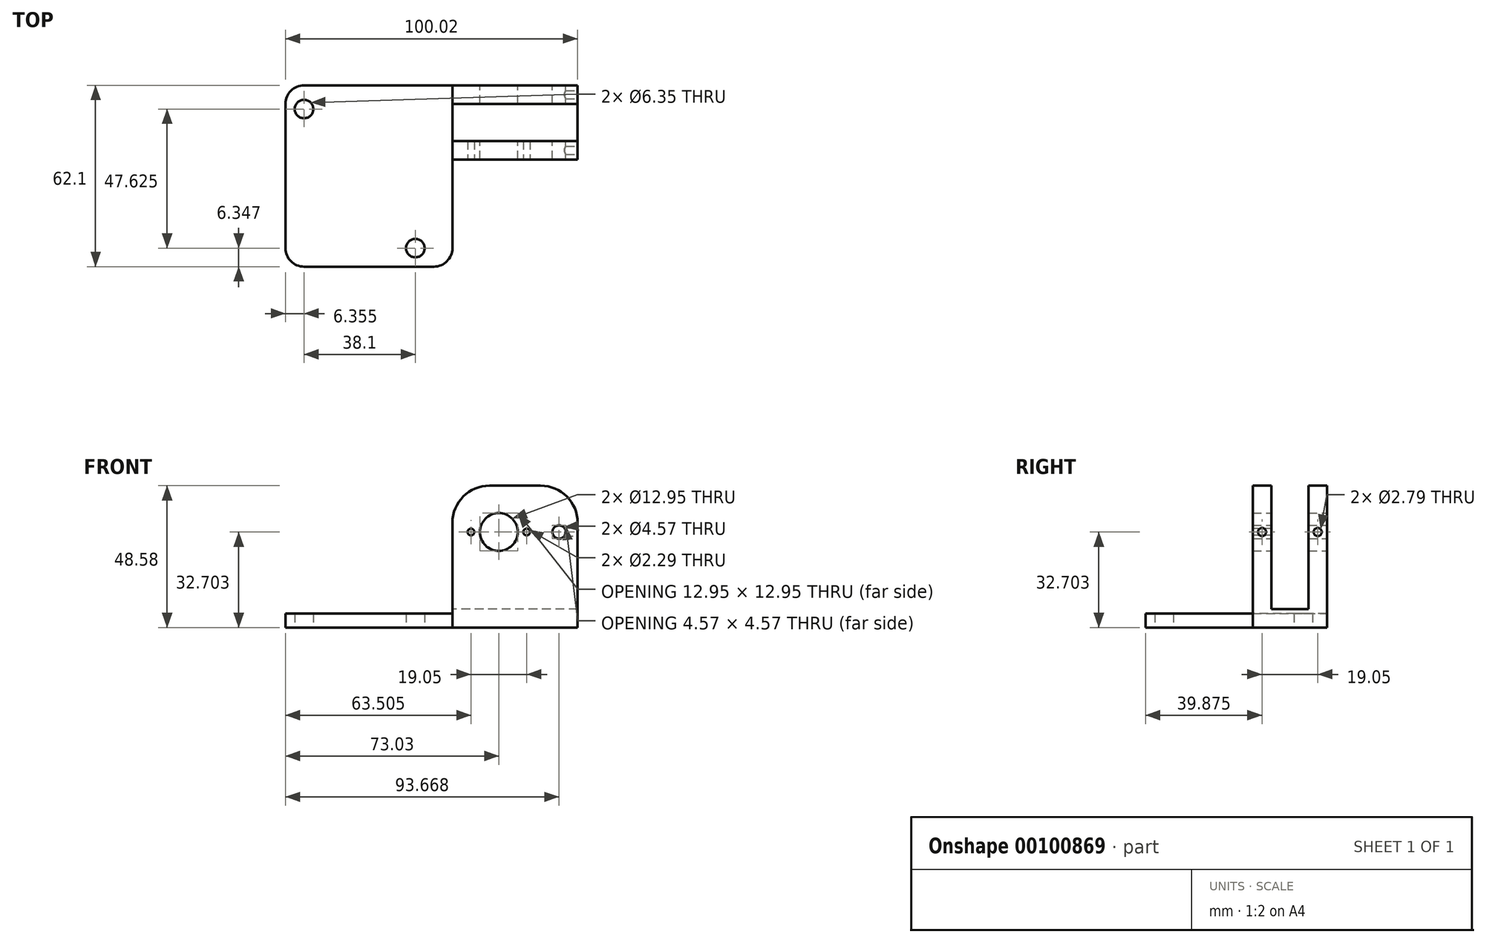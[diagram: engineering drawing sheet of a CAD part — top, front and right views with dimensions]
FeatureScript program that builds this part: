
annotation { "Feature Type Name" : "Feature", "Feature Type Description" : "" }
export const myFeature = defineFeature(function(context is Context, id is Id, definition is map)
    precondition{}
    {
        {
            var Q0;
            Q0=qCreatedBy(makeId("Front.planeOp"),FACE);
            var sketch = newSketch(context, id + "F0", { "sketchPlane" : qUnion([Q0])});
            skCircle(sketch, "E0", {"center": v(0, 32.7) * mm, "radius": 6.48 * mm});
            skLineSegment(sketch, "E1.bottom", {"start": v(-15.87, 0) * mm, "end": v(26.99, 0) * mm});
            skLineSegment(sketch, "E1.top", {"start": v(-3.18, 48.58) * mm, "end": v(14.29, 48.58) * mm});
            skLineSegment(sketch, "E1.left", {"start": v(-15.87, 0) * mm, "end": v(-15.88, 35.88) * mm});
            skLineSegment(sketch, "E1.right", {"start": v(26.99, 0) * mm, "end": v(26.99, 35.88) * mm});
            skCircle(sketch, "E2", {"center": v(20.64, 32.7) * mm, "radius": 2.29 * mm});
            skCircle(sketch, "E3", {"center": v(0, 32.7) * mm, "radius": 20.64 * mm, "construction": true});
            skCircle(sketch, "E4", {"center": v(0, 32.7) * mm, "radius": 12.7 * mm, "construction": true});
            skCircle(sketch, "E5", {"center": v(20.64, 32.7) * mm, "radius": 7.94 * mm, "construction": true});
            skPoint(sketch, "E6.visualSharp", {"position": v(-71.45, 72.7) * mm});
            skPoint(sketch, "E7.visualSharp", {"position": v(-15.88, 48.58) * mm});
            skArc(sketch, "E7.filletArc", {"start": v(-3.18, 48.58) * mm, "mid": v(-12.16, 44.86) * mm, "end": v(-15.88, 35.88) * mm});
            skPoint(sketch, "E8.visualSharp", {"position": v(26.99, 48.58) * mm});
            skArc(sketch, "E8.filletArc", {"start": v(26.99, 35.88) * mm, "mid": v(23.27, 44.86) * mm, "end": v(14.29, 48.58) * mm});
            skSolve(sketch);
        }
        {
            var Q0;
            Q0 = qSketchRegion(id + "F0", true);
            extrude(context, id + "F1", {"entities" : qUnion([Q0]), "depth" : 25.4 * mm});
        }
        {
            var Q0;
            Q0=makeQuery(id+"F1.opExtrude","SWEPT_FACE",FACE,{"disambiguationData":[OSD([sQuery(id+"F0.wireOp",EDGE,"E1.left")])]});
            var sketch = newSketch(context, id + "F2", { "sketchPlane" : qUnion([Q0])});
            skLineSegment(sketch, "E9.bottom", {"start": v(6.35, 60.38) * mm, "end": v(19.05, 60.38) * mm});
            skLineSegment(sketch, "E9.top", {"start": v(6.35, 6.35) * mm, "end": v(19.05, 6.35) * mm});
            skLineSegment(sketch, "E9.left", {"start": v(6.35, 60.38) * mm, "end": v(6.35, 6.35) * mm});
            skLineSegment(sketch, "E9.right", {"start": v(19.05, 60.38) * mm, "end": v(19.05, 6.35) * mm});
            skSolve(sketch);
        }
        {
            var Q0;
            Q0 = qSketchRegion(id + "F2", true);
            extrude(context, id + "F3", {"entities" : qUnion([Q0]), "operationType" : NewBodyOperationType.REMOVE, "endBound" : BoundingType.THROUGH_ALL, "oppositeDirection" : true, "depth" : 25.4 * mm});
        }
        {
            var Q0;
            Q0=qCreatedBy(makeId("Top.planeOp"),FACE);
            var sketch = newSketch(context, id + "F4", { "sketchPlane" : qUnion([Q0])});
            skLineSegment(sketch, "E10", {"start": v(-95.4, -12.7) * mm, "end": v(-15.88, -12.7) * mm, "construction": true});
            skLineSegment(sketch, "E11.MirrorCS", {"start": v(-60.33, -62.1) * mm, "end": v(-28.58, -62.1) * mm, "construction": true});
            skArc(sketch, "E12.MirrorCS", {"start": v(-34.93, -1.78) * mm, "mid": v(-25.94, -5.5) * mm, "end": v(-22.23, -14.48) * mm, "construction": true});
            skLineSegment(sketch, "E13.MirrorCS", {"start": v(-22.22, -55.75) * mm, "end": v(-22.23, -14.48) * mm, "construction": true});
            skArc(sketch, "E14.MirrorCS", {"start": v(-22.22, -55.75) * mm, "mid": v(-24.08, -60.24) * mm, "end": v(-28.58, -62.1) * mm, "construction": true});
            skArc(sketch, "E15.MirrorCS", {"start": v(-60.33, -62.1) * mm, "mid": v(-69.3, -58.38) * mm, "end": v(-73.03, -49.4) * mm, "construction": true});
            skLineSegment(sketch, "E16.MirrorCS", {"start": v(-34.93, -1.78) * mm, "end": v(-66.68, -1.78) * mm, "construction": true});
            skArc(sketch, "E17.MirrorCS", {"start": v(-73.03, -8.13) * mm, "mid": v(-71.17, -3.64) * mm, "end": v(-66.68, -1.78) * mm, "construction": true});
            skLineSegment(sketch, "E18.MirrorCS", {"start": v(-73.03, -8.13) * mm, "end": v(-73.03, -49.4) * mm, "construction": true});
            skCircle(sketch, "E19.MirrorC", {"center": v(-66.68, -8.13) * mm, "radius": 3.18 * mm});
            skCircle(sketch, "E20.MirrorC", {"center": v(-28.57, -55.75) * mm, "radius": 3.18 * mm});
            skLineSegment(sketch, "E21", {"start": v(-15.87, 0) * mm, "end": v(-66.68, 0) * mm});
            skLineSegment(sketch, "E22", {"start": v(-73.03, -6.35) * mm, "end": v(-73.03, -55.75) * mm});
            skLineSegment(sketch, "E23", {"start": v(-66.68, -62.1) * mm, "end": v(-22.22, -62.1) * mm});
            skLineSegment(sketch, "E24", {"start": v(-15.87, -55.75) * mm, "end": v(-15.87, 0) * mm});
            skPoint(sketch, "E25.visualSharp", {"position": v(-15.88, -62.1) * mm});
            skArc(sketch, "E25.filletArc", {"start": v(-22.22, -62.1) * mm, "mid": v(-17.73, -60.24) * mm, "end": v(-15.87, -55.75) * mm});
            skPoint(sketch, "E26.visualSharp", {"position": v(-73.03, -62.1) * mm});
            skArc(sketch, "E26.filletArc", {"start": v(-73.03, -55.75) * mm, "mid": v(-71.17, -60.24) * mm, "end": v(-66.68, -62.1) * mm});
            skPoint(sketch, "E27.visualSharp", {"position": v(-73.03, 0) * mm});
            skArc(sketch, "E27.filletArc", {"start": v(-66.68, 0) * mm, "mid": v(-71.17, -1.86) * mm, "end": v(-73.03, -6.35) * mm});
            skSolve(sketch);
        }
        {
            var Q0;
            Q0 = qSketchRegion(id + "F4", true);
            extrude(context, id + "F5", {"entities" : qUnion([Q0]), "operationType" : NewBodyOperationType.ADD, "depth" : 4.76 * mm});
        }
        {
            var Q0;
            Q0=makeQuery(id+"F1.opExtrude","CAP_FACE",FACE,{"disambiguationData":[OSD([sQuery(id+"F0.wireOp",EDGE,"E0"),sQuery(id+"F0.wireOp",EDGE,"E1.bottom"),sQuery(id+"F0.wireOp",EDGE,"E1.top"),sQuery(id+"F0.wireOp",EDGE,"E1.left"),sQuery(id+"F0.wireOp",EDGE,"E1.right"),sQuery(id+"F0.wireOp",EDGE,"E2"),sQuery(id+"F0.wireOp",EDGE,"E7.filletArc"),sQuery(id+"F0.wireOp",EDGE,"E8.filletArc")])],"isStart":false});
            var sketch = newSketch(context, id + "F6", { "sketchPlane" : qUnion([Q0])});
            skCircle(sketch, "E28", {"center": v(9.52, 32.7) * mm, "radius": 1.14 * mm});
            skCircle(sketch, "E29", {"center": v(-9.53, 32.7) * mm, "radius": 1.14 * mm});
            skLineSegment(sketch, "E30", {"start": v(-9.53, 32.7) * mm, "end": v(9.52, 32.7) * mm, "construction": true});
            skPoint(sketch, "E31", {"position": v(0, 32.7) * mm});
            skSolve(sketch);
        }
        {
            var Q0;
            Q0 = qSketchRegion(id + "F6", true);
            extrude(context, id + "F7", {"entities" : qUnion([Q0]), "operationType" : NewBodyOperationType.REMOVE, "endBound" : BoundingType.UP_TO_NEXT, "oppositeDirection" : true, "depth" : 25.4 * mm});
        }
        {
            var Q0;
            Q0=makeQuery(id+"F1.opExtrude","SWEPT_FACE",FACE,{"disambiguationData":[OSD([sQuery(id+"F0.wireOp",EDGE,"E1.right")])]});
            var sketch = newSketch(context, id + "F8", { "sketchPlane" : qUnion([Q0])});
            skCircle(sketch, "E32", {"center": v(-22.23, 32.7) * mm, "radius": 1.4 * mm});
            skCircle(sketch, "E33", {"center": v(-3.18, 32.7) * mm, "radius": 1.4 * mm});
            skSolve(sketch);
        }
        {
            var Q0;
            Q0 = qSketchRegion(id + "F8", true);
            extrude(context, id + "F9", {"entities" : qUnion([Q0]), "operationType" : NewBodyOperationType.REMOVE, "endBound" : BoundingType.UP_TO_NEXT, "oppositeDirection" : true, "depth" : 25.4 * mm});
        }
    });
